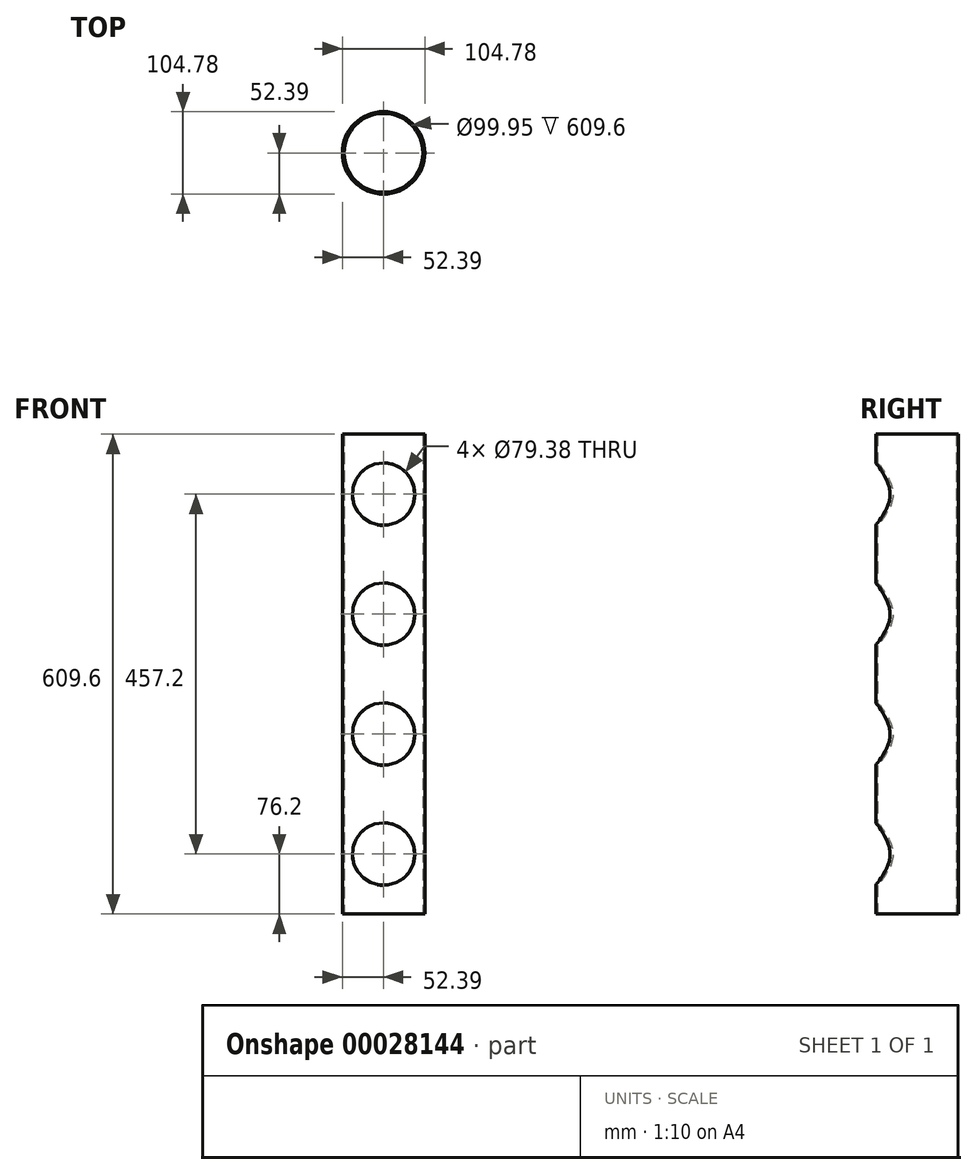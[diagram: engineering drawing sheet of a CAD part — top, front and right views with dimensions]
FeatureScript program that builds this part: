
annotation { "Feature Type Name" : "Feature", "Feature Type Description" : "" }
export const myFeature = defineFeature(function(context is Context, id is Id, definition is map)
    precondition{}
    {
        {
            var Q0;
            Q0=qCreatedBy(makeId("Top.planeOp"),FACE);
            var sketch = newSketch(context, id + "F0", { "sketchPlane" : qUnion([Q0])});
            skCircle(sketch, "E0", {"center": v(0, 0) * mm, "radius": 52.39 * mm});
            skSolve(sketch);
        }
        {
            var Q0;
            Q0=makeQuery(id+"F0.imprint","IMPRINT",FACE,{"disambiguationData":[TD([[makeQuery(id+"F0.imprint","IMPRINT",EDGE,{"derivedFrom":sQuery(id+"F0.wireOp",EDGE,"E0")}),1.0]])]});
            var Q1;
            Q1=sQuery(id+"F0.wireOp",EDGE,"E0");
            extrude(context, id + "F1", {"entities" : qUnion([Q0]), "surfaceEntities" : qUnion([Q1]), "depth" : 609.6 * mm});
        }
        {
            var Q0;
            Q0=makeQuery(id+"F1.opExtrude","CAP_FACE",FACE,{"disambiguationData":[OSD([sQuery(id+"F0.wireOp",EDGE,"E0")])],"isStart":false});
            var Q1;
            Q1=makeQuery(id+"F1.opExtrude","CAP_FACE",FACE,{"disambiguationData":[OSD([sQuery(id+"F0.wireOp",EDGE,"E0")])],"isStart":true});
            shell(context, id + "F2", {"entities" : qUnion([Q0, Q1]), "thickness" : 2.41 * mm});
        }
        {
            var Q0;
            Q0=qCreatedBy(makeId("Front.planeOp"),FACE);
            var sketch = newSketch(context, id + "F3", { "sketchPlane" : qUnion([Q0])});
            skLineSegment(sketch, "E1", {"start": v(0, 0) * mm, "end": v(0, 610.38) * mm, "construction": true});
            skPoint(sketch, "E2", {"position": v(0, 76.2) * mm});
            skPoint(sketch, "E3", {"position": v(0, 228.6) * mm});
            skPoint(sketch, "E4", {"position": v(0, 381) * mm});
            skPoint(sketch, "E5", {"position": v(0, 533.4) * mm});
            skLineSegment(sketch, "E6.direction1", {"start": v(0, 0) * mm, "end": v(25.4, 0) * mm, "construction": true});
            skCircle(sketch, "E7", {"center": v(0, 76.2) * mm, "radius": 39.69 * mm});
            skCircle(sketch, "E8", {"center": v(0, 228.6) * mm, "radius": 39.69 * mm});
            skCircle(sketch, "E9", {"center": v(0, 381) * mm, "radius": 39.69 * mm});
            skCircle(sketch, "E10", {"center": v(0, 533.4) * mm, "radius": 39.69 * mm});
            skSolve(sketch);
        }
        {
            var Q0;
            Q0 = qSketchRegion(id + "F3", true);
            extrude(context, id + "F4", {"entities" : qUnion([Q0]), "operationType" : NewBodyOperationType.REMOVE, "depth" : 76.2 * mm});
        }
    });
